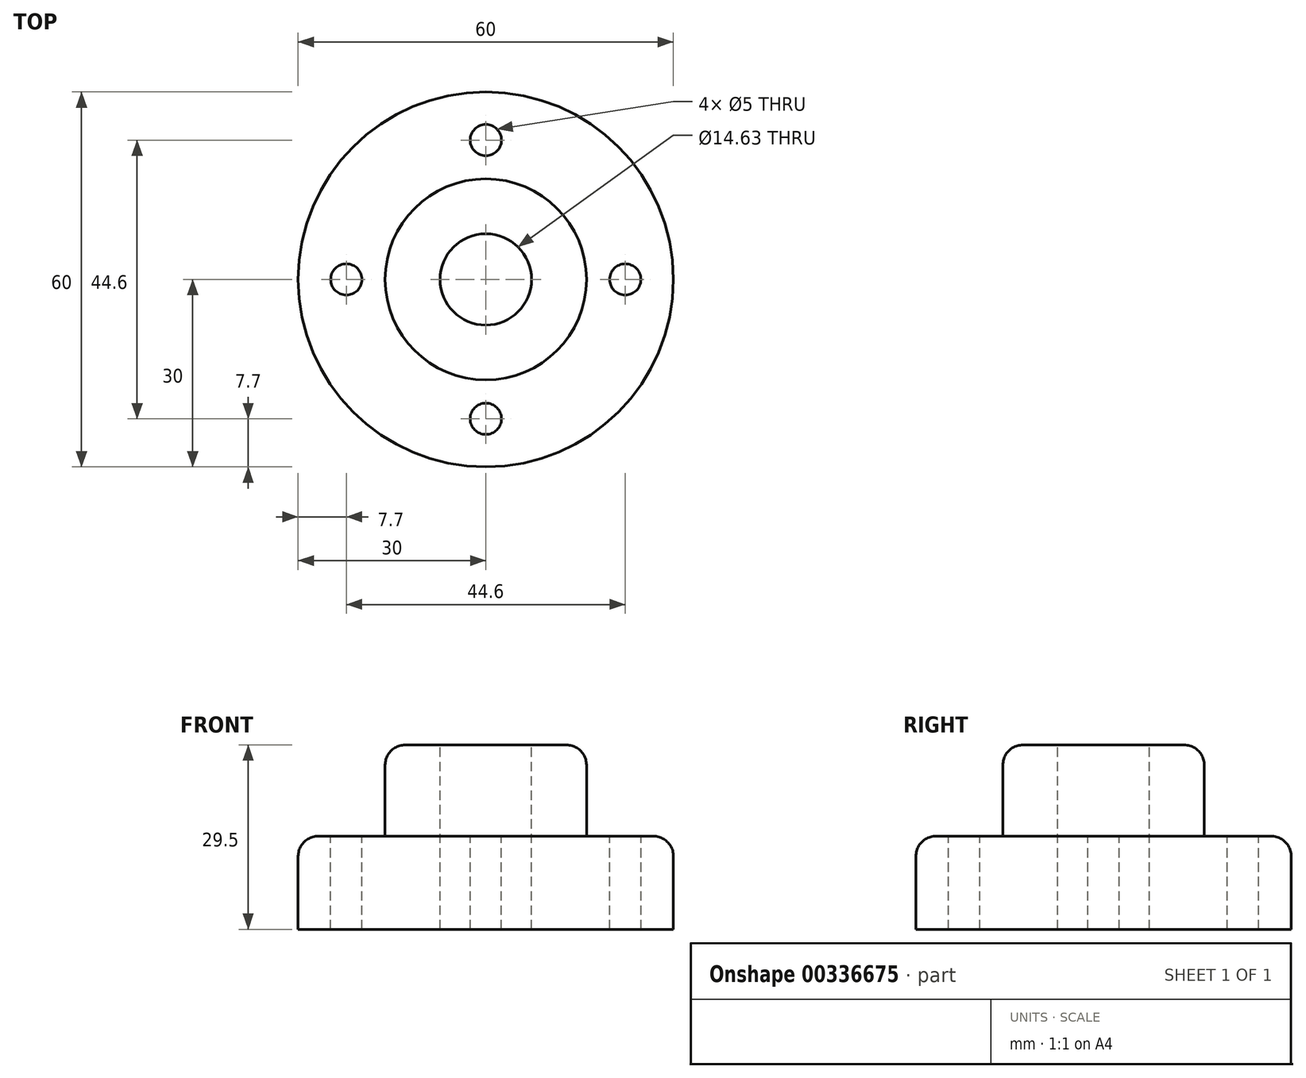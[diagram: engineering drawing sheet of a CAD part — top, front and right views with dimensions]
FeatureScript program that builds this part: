
annotation { "Feature Type Name" : "Feature", "Feature Type Description" : "" }
export const myFeature = defineFeature(function(context is Context, id is Id, definition is map)
    precondition{}
    {
        {
            var Q0;
            Q0=qCreatedBy(makeId("Top.planeOp"),FACE);
            var sketch = newSketch(context, id + "F0", { "sketchPlane" : qUnion([Q0])});
            skCircle(sketch, "E0", {"center": v(0, 0) * mm, "radius": 30 * mm});
            skCircle(sketch, "E1", {"center": v(0, 0) * mm, "radius": 16.1 * mm});
            skCircle(sketch, "E2", {"center": v(0, 0) * mm, "radius": 7.32 * mm});
            skCircle(sketch, "E3", {"center": v(-22.3, 0) * mm, "radius": 2.5 * mm});
            skCircle(sketch, "E4", {"center": v(0, -22.3) * mm, "radius": 2.5 * mm});
            skCircle(sketch, "E5", {"center": v(22.3, 0) * mm, "radius": 2.5 * mm});
            skCircle(sketch, "E6", {"center": v(0, 22.3) * mm, "radius": 2.5 * mm});
            skSolve(sketch);
        }
        {
            var Q0;
            Q0 = qSketchRegion(id + "F0", true);
            var Q1;
            Q1=makeQuery(id+"F0.imprint","IMPRINT",FACE,{"disambiguationData":[TD([[makeQuery(id+"F0.imprint","IMPRINT",EDGE,{"derivedFrom":sQuery(id+"F0.wireOp",EDGE,"E1")}),1.0]])]});
            extrude(context, id + "F1", {"entities" : qUnion([Q0, Q1]), "oppositeDirection" : true, "depth" : 14.9 * mm});
        }
        {
            var Q0;
            Q0=makeQuery(id+"F1.opExtrude","CAP_EDGE",EDGE,{"disambiguationData":[OSD([sQuery(id+"F0.wireOp",EDGE,"E0")])],"isStart":true});
            fillet(context, id + "F2", {"entities" : qUnion([Q0]), "radius" : 3.2 * mm, "tangentPropagation" : true, "allowEdgeOverflow" : false});
        }
        {
            var Q0;
            Q0=makeQuery(id+"F0.imprint","IMPRINT",FACE,{"disambiguationData":[TD([[makeQuery(id+"F0.imprint","IMPRINT",EDGE,{"derivedFrom":sQuery(id+"F0.wireOp",EDGE,"E1")}),1.0]])]});
            extrude(context, id + "F3", {"entities" : qUnion([Q0]), "operationType" : NewBodyOperationType.ADD, "depth" : 14.6 * mm});
        }
        {
            var Q0;
            Q0=makeQuery(id+"F3.opExtrude","CAP_EDGE",EDGE,{"disambiguationData":[OSD([sQuery(id+"F0.wireOp",EDGE,"E1")])],"isStart":false});
            fillet(context, id + "F4", {"entities" : qUnion([Q0]), "radius" : 3.2 * mm, "tangentPropagation" : true, "allowEdgeOverflow" : false});
        }
    });
